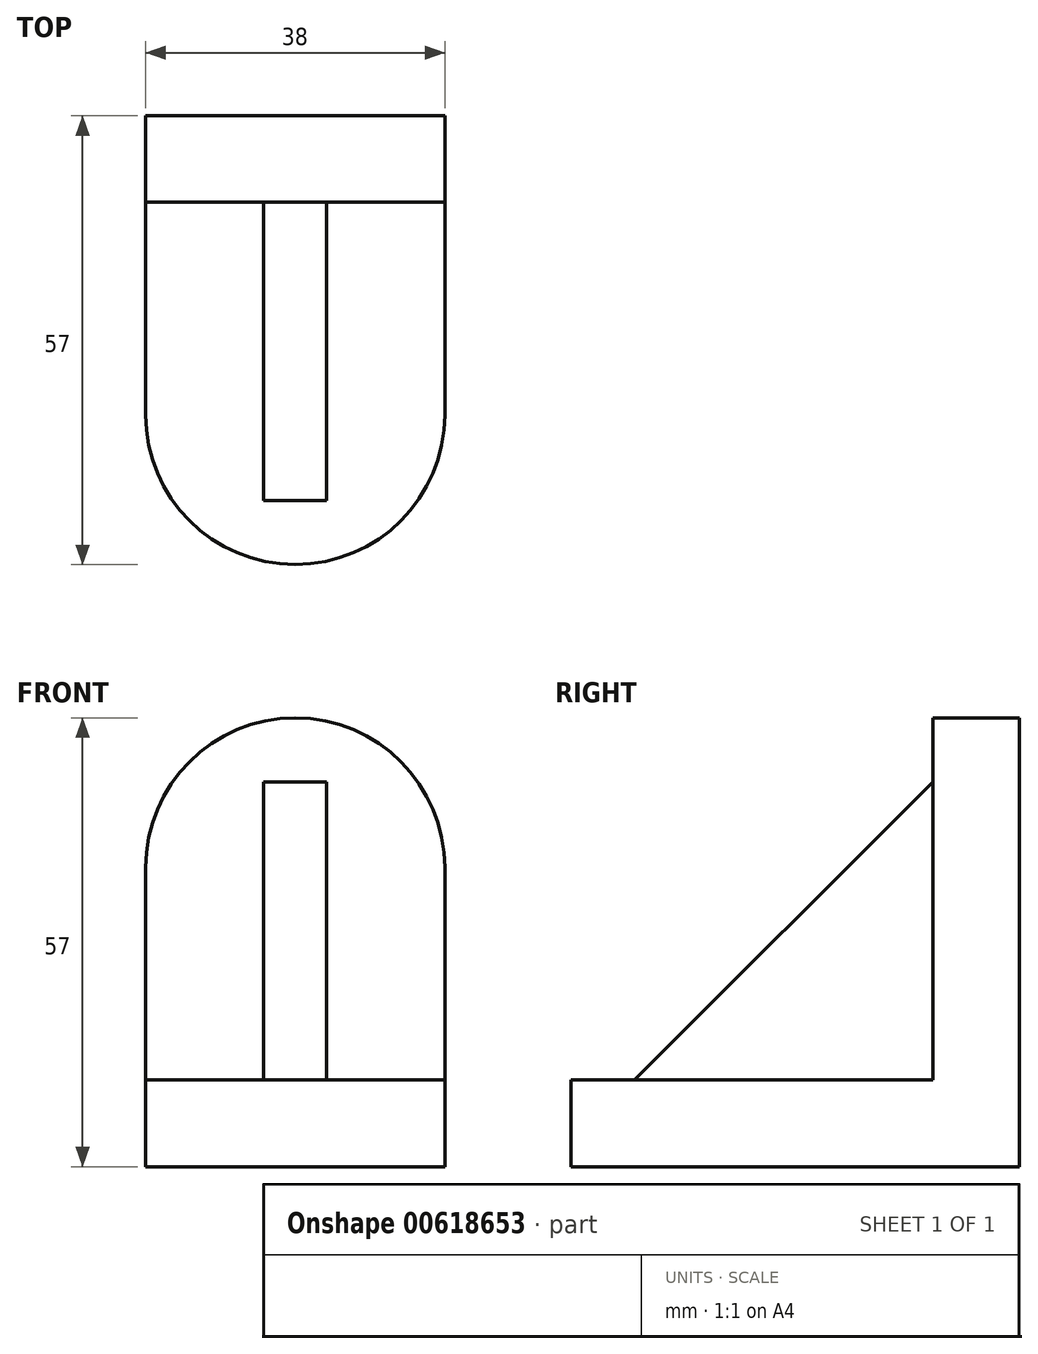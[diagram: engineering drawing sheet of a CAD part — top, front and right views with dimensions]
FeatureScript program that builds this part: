
annotation { "Feature Type Name" : "Feature", "Feature Type Description" : "" }
export const myFeature = defineFeature(function(context is Context, id is Id, definition is map)
    precondition{}
    {
        {
            var Q0;
            Q0=qCreatedBy(makeId("Front.planeOp"),FACE);
            var sketch = newSketch(context, id + "F0", { "sketchPlane" : qUnion([Q0])});
            skLineSegment(sketch, "E0", {"start": v(0, 0) * mm, "end": v(0, 38) * mm});
            skLineSegment(sketch, "E1", {"start": v(38, 38) * mm, "end": v(38, 0) * mm});
            skLineSegment(sketch, "E2", {"start": v(0, 0) * mm, "end": v(38, 0) * mm});
            skArc(sketch, "E3", {"start": v(38, 38) * mm, "mid": v(19, 57) * mm, "end": v(0, 38) * mm});
            skSolve(sketch);
        }
        {
            var Q0;
            Q0=makeQuery(id+"F0.imprint","IMPRINT",FACE,{"disambiguationData":[TD([[makeQuery(id+"F0.imprint","IMPRINT",EDGE,{"derivedFrom":sQuery(id+"F0.wireOp",EDGE,"E0")}),-1.0]])]});
            extrude(context, id + "F1", {"entities" : qUnion([Q0]), "depth" : 11 * mm, "offsetDistance" : 25 * mm});
        }
        {
            var Q0;
            Q0=qCreatedBy(makeId("Top.planeOp"),FACE);
            var sketch = newSketch(context, id + "F2", { "sketchPlane" : qUnion([Q0])});
            skLineSegment(sketch, "E4", {"start": v(0, 0) * mm, "end": v(0, -38) * mm});
            skLineSegment(sketch, "E5", {"start": v(38, -38) * mm, "end": v(38, 0) * mm});
            skLineSegment(sketch, "E6", {"start": v(0, 0) * mm, "end": v(38, 0) * mm});
            skArc(sketch, "E7", {"start": v(0, -38) * mm, "mid": v(19, -57) * mm, "end": v(38, -38) * mm});
            skSolve(sketch);
        }
        {
            var Q0;
            Q0=makeQuery(id+"F2.imprint","IMPRINT",FACE,{"disambiguationData":[TD([[makeQuery(id+"F2.imprint","IMPRINT",EDGE,{"derivedFrom":sQuery(id+"F2.wireOp",EDGE,"E4")}),1.0]])]});
            extrude(context, id + "F3", {"entities" : qUnion([Q0]), "operationType" : NewBodyOperationType.ADD, "depth" : 11 * mm, "offsetDistance" : 25 * mm});
        }
        {
            var Q0;
            Q0=makeQuery(id+"F1.opExtrude","CAP_FACE",FACE,{"disambiguationData":[OSD([sQuery(id+"F0.wireOp",EDGE,"E0"),sQuery(id+"F0.wireOp",EDGE,"E1"),sQuery(id+"F0.wireOp",EDGE,"E2"),sQuery(id+"F0.wireOp",EDGE,"E3")])],"isStart":false});
            cPlane(context, id + "F4", {"entities" : qUnion([Q0]), "cplaneType" : CPlaneType.OFFSET, "offset" : 0 * mm, "width" : 150 * mm, "height" : 150 * mm});
        }
        {
            var Q0;
            Q0=qCreatedBy(id+"F4.planeOp",FACE);
            var sketch = newSketch(context, id + "F5", { "sketchPlane" : qUnion([Q0])});
            skLineSegment(sketch, "E8", {"start": v(15, 10.9) * mm, "end": v(15, 48.9) * mm});
            skLineSegment(sketch, "E9", {"start": v(15, 48.9) * mm, "end": v(23, 48.9) * mm});
            skLineSegment(sketch, "E10", {"start": v(23, 48.9) * mm, "end": v(23, 10.9) * mm});
            skLineSegment(sketch, "E11", {"start": v(15, 10.9) * mm, "end": v(23, 10.9) * mm});
            skSolve(sketch);
        }
        {
            var Q0;
            Q0 = qSketchRegion(id + "F5", true);
            extrude(context, id + "F6", {"entities" : qUnion([Q0]), "operationType" : NewBodyOperationType.ADD, "depth" : 38 * mm, "offsetDistance" : 25 * mm});
        }
        {
            var Q0;
            Q0=makeQuery(id+"F6.opExtrude","CAP_EDGE",EDGE,{"disambiguationData":[OSD([sQuery(id+"F5.wireOp",EDGE,"E9")])],"isStart":false});
            chamfer(context, id + "F7", {"entities" : qUnion([Q0]), "width" : 38 * mm, "tangentPropagation" : true});
        }
    });
